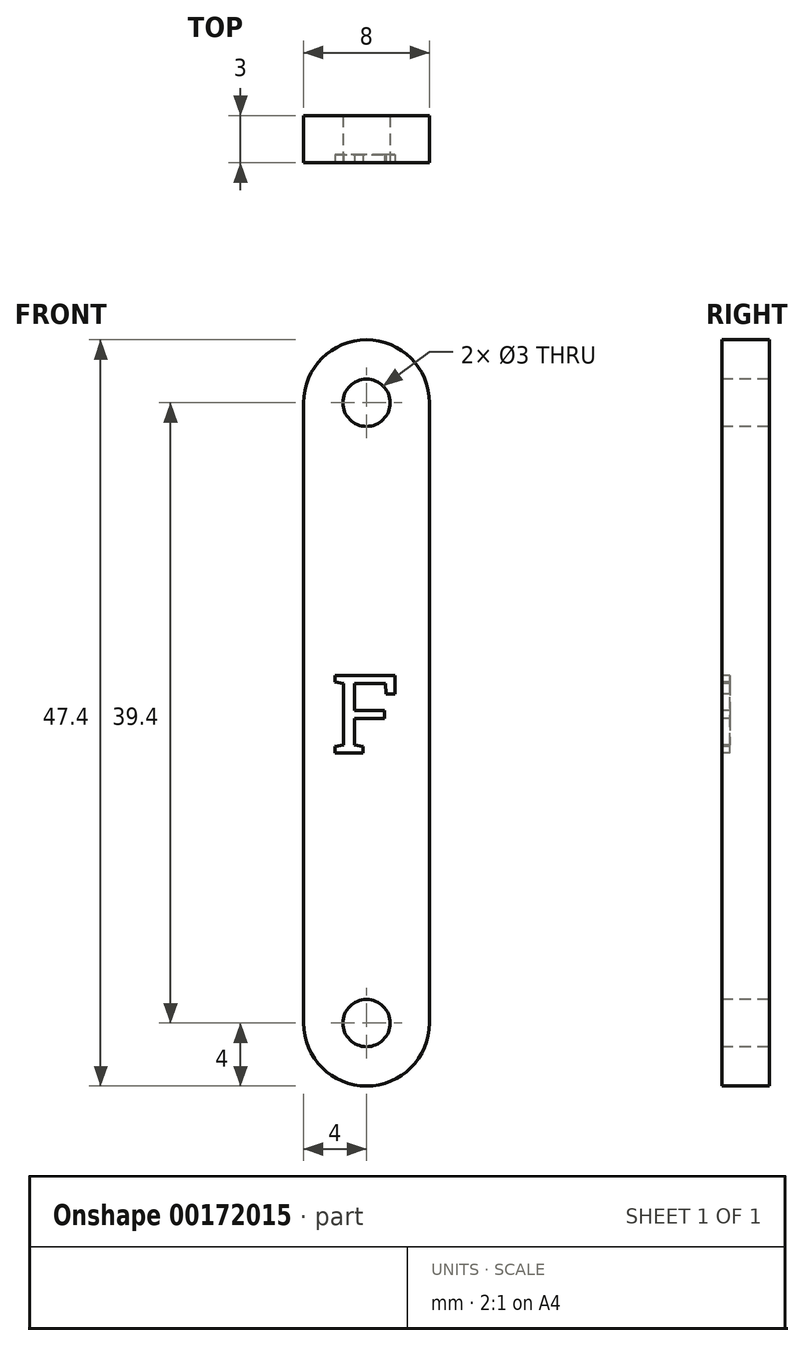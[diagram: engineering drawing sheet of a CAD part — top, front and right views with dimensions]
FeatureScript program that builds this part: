
annotation { "Feature Type Name" : "Feature", "Feature Type Description" : "" }
export const myFeature = defineFeature(function(context is Context, id is Id, definition is map)
    precondition{}
    {
        {
            assignVariable(context, id + "F0", {"name" : "Thickness", "anyValue" : 3});
        }
        {
            var Q0;
            Q0=qCreatedBy(makeId("Front.planeOp"),FACE);
            var sketch = newSketch(context, id + "F1", { "sketchPlane" : qUnion([Q0])});
            skCircle(sketch, "E0", {"center": v(0, 39.4) * mm, "radius": 1.5 * mm});
            skCircle(sketch, "E1", {"center": v(0, 0) * mm, "radius": 1.5 * mm});
            skArc(sketch, "E2", {"start": v(4, 39.4) * mm, "mid": v(0, 43.4) * mm, "end": v(-4, 39.4) * mm});
            skArc(sketch, "E3", {"start": v(-4, 0) * mm, "mid": v(0, -4) * mm, "end": v(4, 0) * mm});
            skLineSegment(sketch, "E4", {"start": v(-4, 0) * mm, "end": v(-4, 39.4) * mm});
            skLineSegment(sketch, "E5", {"start": v(4, 39.4) * mm, "end": v(4, 0) * mm});
            skSolve(sketch);
        }
        {
            var Q0;
            Q0=makeQuery(id+"F1.imprint","IMPRINT",FACE,{"disambiguationData":[TD([[makeQuery(id+"F1.imprint","IMPRINT",EDGE,{"derivedFrom":sQuery(id+"F1.wireOp",EDGE,"E0")}),-1.0]])]});
            extrude(context, id + "F2", {"entities" : qUnion([Q0]), "oppositeDirection" : true, "depth" : (getVariable(context, 'Thickness')) * mm});
        }
        {
            var Q0;
            Q0=qCreatedBy(makeId("Front.planeOp"),FACE);
            var sketch = newSketch(context, id + "F3", { "sketchPlane" : qUnion([Q0])});
            skText(sketch, "E6", { "text": "F", "fontName": "RobotoSlab-Regular.ttf"});
            skLineSegment(sketch, "E7", {"start": v(4, 19.7) * mm, "end": v(1.35, 19.7) * mm, "construction": true});
            const initialGuessF3  = {"E6": [-0.00224, 0.01715, 1, 0, 0.005]};
            skSetInitialGuess(sketch, initialGuessF3);
            skSolve(sketch);
        }
        {
            assignVariable(context, id + "F4", {"name" : "DepthText", "anyValue" : .5});
        }
        {
            var Q0;
            Q0=qSketchRegion(id+"F3",true);
            extrude(context, id + "F5", {"entities" : qUnion([Q0]), "operationType" : NewBodyOperationType.REMOVE, "oppositeDirection" : true, "depth" : (getVariable(context, 'DepthText')) * mm});
        }
    });
